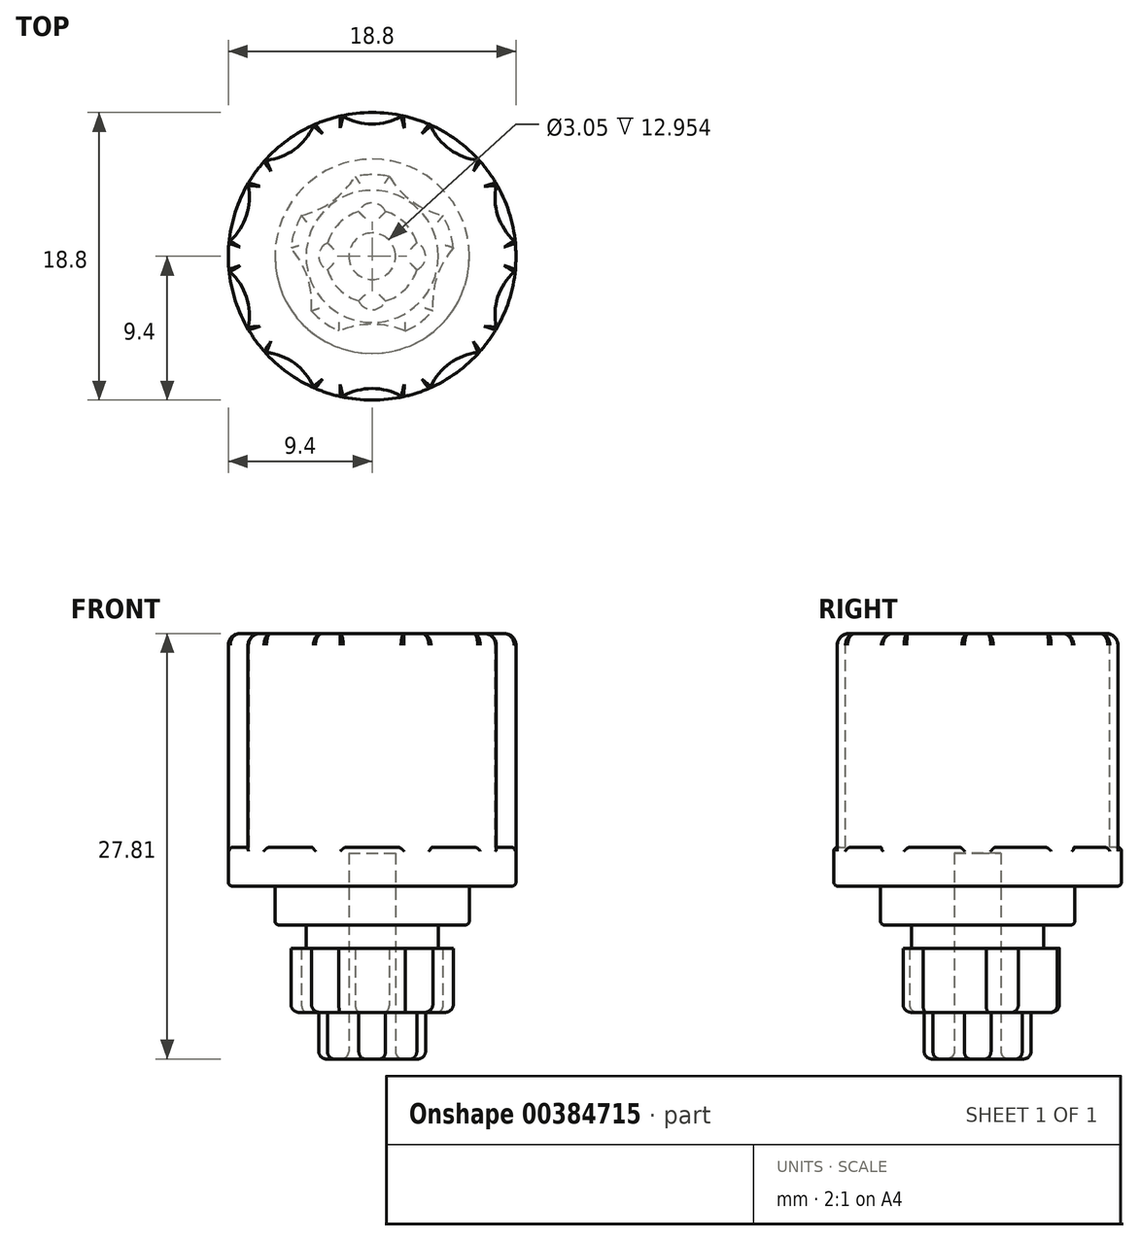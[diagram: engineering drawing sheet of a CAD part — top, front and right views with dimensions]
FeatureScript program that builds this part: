
annotation { "Feature Type Name" : "Feature", "Feature Type Description" : "" }
export const myFeature = defineFeature(function(context is Context, id is Id, definition is map)
    precondition{}
    {
        {
            var Q0;
            Q0=qCreatedBy(makeId("Top.planeOp"),FACE);
            var sketch = newSketch(context, id + "F0", { "sketchPlane" : qUnion([Q0])});
            skCircle(sketch, "E0", {"center": v(0, 0) * mm, "radius": 9.4 * mm});
            skSolve(sketch);
        }
        {
            var Q0;
            Q0=qSketchRegion(id+"F0",true);
            extrude(context, id + "F1", {"entities" : qUnion([Q0]), "depth" : 16.5 * mm});
        }
        {
            var Q0;
            Q0=makeQuery(id+"F1.opExtrude","CAP_FACE",FACE,{"disambiguationData":[OSD([sQuery(id+"F0.wireOp",EDGE,"E0")])],"isStart":false});
            var sketch = newSketch(context, id + "F2", { "sketchPlane" : qUnion([Q0])});
            skCircle(sketch, "E1.1.0", {"center": v(-7.32, 10.07) * mm, "radius": 3.81 * mm});
            skCircle(sketch, "E1.2.0", {"center": v(-11.84, 3.85) * mm, "radius": 3.81 * mm});
            skCircle(sketch, "E1.3.0", {"center": v(-11.84, -3.85) * mm, "radius": 3.81 * mm});
            skCircle(sketch, "E1.4.0", {"center": v(-7.32, -10.07) * mm, "radius": 3.81 * mm});
            skCircle(sketch, "E1.5.0", {"center": v(0, -12.45) * mm, "radius": 3.81 * mm});
            skCircle(sketch, "E1.6.0", {"center": v(7.32, -10.07) * mm, "radius": 3.81 * mm});
            skCircle(sketch, "E1.7.0", {"center": v(11.84, -3.85) * mm, "radius": 3.81 * mm});
            skCircle(sketch, "E1.8.0", {"center": v(11.84, 3.85) * mm, "radius": 3.81 * mm});
            skCircle(sketch, "E1.9.0", {"center": v(7.32, 10.07) * mm, "radius": 3.81 * mm});
            skPoint(sketch, "E1.center", {"position": v(0, 0) * mm});
            skPoint(sketch, "E2.center.orphan", {"position": v(0, 12.45) * mm});
            skCircle(sketch, "E3", {"center": v(0, 12.45) * mm, "radius": 3.81 * mm});
            skSolve(sketch);
        }
        {
            var Q0;
            Q0=qSketchRegion(id+"F2",true);
            extrude(context, id + "F3", {"entities" : qUnion([Q0]), "operationType" : NewBodyOperationType.REMOVE, "oppositeDirection" : true, "depth" : 13.97 * mm});
        }
        {
            var Q0;
            Q0=makeQuery(id+"F1.opExtrude","CAP_FACE",FACE,{"disambiguationData":[OSD([sQuery(id+"F0.wireOp",EDGE,"E0")])],"isStart":false});
            fillet(context, id + "F4", {"entities" : qUnion([Q0]), "radius" : 0.76 * mm, "tangentPropagation" : true, "allowEdgeOverflow" : false});
        }
        {
            var Q0;
            Q0=makeQuery(id+"F1.opExtrude","CAP_FACE",FACE,{"disambiguationData":[OSD([sQuery(id+"F0.wireOp",EDGE,"E0")])],"isStart":true});
            var sketch = newSketch(context, id + "F5", { "sketchPlane" : qUnion([Q0])});
            skCircle(sketch, "E4", {"center": v(0, 0) * mm, "radius": 5.33 * mm});
            skSolve(sketch);
        }
        {
            var Q0;
            Q0=qSketchRegion(id+"F5",true);
            extrude(context, id + "F6", {"entities" : qUnion([Q0]), "operationType" : NewBodyOperationType.ADD, "depth" : 8.25 * mm, "offsetDistance" : 25.4 * mm});
        }
        {
            var Q0;
            Q0=makeQuery(id+"F6.opExtrude","CAP_FACE",FACE,{"disambiguationData":[OSD([sQuery(id+"F5.wireOp",EDGE,"E4")])],"isStart":false});
            var sketch = newSketch(context, id + "F7", { "sketchPlane" : qUnion([Q0])});
            skCircle(sketch, "E5", {"center": v(0, 10.16) * mm, "radius": 5.72 * mm});
            skCircle(sketch, "E6.1.0", {"center": v(-9.66, 3.14) * mm, "radius": 5.72 * mm});
            skCircle(sketch, "E6.2.0", {"center": v(-5.97, -8.22) * mm, "radius": 5.72 * mm});
            skCircle(sketch, "E6.3.0", {"center": v(5.97, -8.22) * mm, "radius": 5.72 * mm});
            skCircle(sketch, "E6.4.0", {"center": v(9.66, 3.14) * mm, "radius": 5.72 * mm});
            skPoint(sketch, "E6.center", {"position": v(0, 0) * mm});
            skSolve(sketch);
        }
        {
            var Q0;
            Q0=qSketchRegion(id+"F7",true);
            extrude(context, id + "F8", {"entities" : qUnion([Q0]), "operationType" : NewBodyOperationType.REMOVE, "oppositeDirection" : true, "depth" : 7.62 * mm});
        }
        {
            var Q0;
            Q0=makeQuery(id+"F8.boolean.opBoolean","MERGE",FACE,{"derivedFrom":[makeQuery(id+"F1.opExtrude","CAP_FACE",FACE,{"disambiguationData":[OSD([sQuery(id+"F0.wireOp",EDGE,"E0")])],"isStart":true}),makeQuery(id+"F8.opExtrude","CAP_FACE",FACE,{"disambiguationData":[OSD([sQuery(id+"F7.wireOp",EDGE,"E5")])],"isStart":false}),makeQuery(id+"F8.opExtrude","CAP_FACE",FACE,{"disambiguationData":[OSD([sQuery(id+"F7.wireOp",EDGE,"E6.1.0")])],"isStart":false}),makeQuery(id+"F8.opExtrude","CAP_FACE",FACE,{"disambiguationData":[OSD([sQuery(id+"F7.wireOp",EDGE,"E6.2.0")])],"isStart":false}),makeQuery(id+"F8.opExtrude","CAP_FACE",FACE,{"disambiguationData":[OSD([sQuery(id+"F7.wireOp",EDGE,"E6.3.0")])],"isStart":false}),makeQuery(id+"F8.opExtrude","CAP_FACE",FACE,{"disambiguationData":[OSD([sQuery(id+"F7.wireOp",EDGE,"E6.4.0")])],"isStart":false})]});
            var sketch = newSketch(context, id + "F9", { "sketchPlane" : qUnion([Q0])});
            skCircle(sketch, "E7", {"center": v(0, 0) * mm, "radius": 6.22 * mm});
            skCircle(sketch, "E8", {"center": v(0, 0) * mm, "radius": 4.32 * mm});
            skSolve(sketch);
        }
        {
            var Q0;
            Q0=qSketchRegion(id+"F9",true);
            extrude(context, id + "F10", {"entities" : qUnion([Q0]), "operationType" : NewBodyOperationType.REMOVE, "depth" : 4.06 * mm, "offsetDistance" : 25.4 * mm});
        }
        {
            var Q0;
            Q0=makeQuery(id+"F10.boolean.opBoolean","MERGE",FACE,{"derivedFrom":[makeQuery(id+"F1.opExtrude","CAP_FACE",FACE,{"disambiguationData":[OSD([sQuery(id+"F0.wireOp",EDGE,"E0")])],"isStart":true}),makeQuery(id+"F10.opExtrude","CAP_FACE",FACE,{"disambiguationData":[OSD([sQuery(id+"F9.wireOp",EDGE,"E7"),sQuery(id+"F9.wireOp",EDGE,"E8")])],"isStart":true})]});
            var sketch = newSketch(context, id + "F11", { "sketchPlane" : qUnion([Q0])});
            skCircle(sketch, "E9", {"center": v(0, 0) * mm, "radius": 6.35 * mm});
            skSolve(sketch);
        }
        {
            var Q0;
            Q0=qSketchRegion(id+"F11",true);
            extrude(context, id + "F12", {"entities" : qUnion([Q0]), "operationType" : NewBodyOperationType.ADD, "depth" : 2.54 * mm, "offsetDistance" : 25.4 * mm});
        }
        {
            var Q0;
            Q0=makeQuery(id+"F6.opExtrude","CAP_FACE",FACE,{"disambiguationData":[OSD([sQuery(id+"F5.wireOp",EDGE,"E4")])],"isStart":false});
            fillet(context, id + "F13", {"entities" : qUnion([Q0]), "radius" : 0.5 * mm, "tangentPropagation" : true, "allowEdgeOverflow" : false});
        }
        {
            var Q0;
            Q0=makeQuery(id+"F12.opExtrude","CAP_EDGE",EDGE,{"disambiguationData":[OSD([sQuery(id+"F11.wireOp",EDGE,"E9")])],"isStart":false});
            var Q1;
            Q1=makeQuery(id+"F1.opExtrude","CAP_EDGE",EDGE,{"disambiguationData":[OSD([sQuery(id+"F0.wireOp",EDGE,"E0")])],"isStart":true});
            var Q2;
            Q2=makeQuery(id+"F3.boolean.opBoolean","INTERSECT",EDGE,{"derivedFrom":[makeQuery(id+"F1.opExtrude","SWEPT_FACE",FACE,{"disambiguationData":[OSD([sQuery(id+"F0.wireOp",EDGE,"E0")])]}),makeQuery(id+"F3.opExtrude","CAP_FACE",FACE,{"disambiguationData":[OSD([sQuery(id+"F2.wireOp",EDGE,"E1.4.0")])],"isStart":false})]});
            var Q3;
            Q3=makeQuery(id+"F3.boolean.opBoolean","INTERSECT",EDGE,{"derivedFrom":[makeQuery(id+"F1.opExtrude","SWEPT_FACE",FACE,{"disambiguationData":[OSD([sQuery(id+"F0.wireOp",EDGE,"E0")])]}),makeQuery(id+"F3.opExtrude","CAP_FACE",FACE,{"disambiguationData":[OSD([sQuery(id+"F2.wireOp",EDGE,"E1.5.0")])],"isStart":false})]});
            var Q4;
            Q4=makeQuery(id+"F3.boolean.opBoolean","INTERSECT",EDGE,{"disambiguationData":[OD(0.0)],"derivedFrom":[makeQuery(id+"F1.opExtrude","SWEPT_FACE",FACE,{"disambiguationData":[OSD([sQuery(id+"F0.wireOp",EDGE,"E0")])]}),makeQuery(id+"F3.opExtrude","SWEPT_FACE",FACE,{"disambiguationData":[OSD([sQuery(id+"F2.wireOp",EDGE,"E1.4.0")])]})]});
            var Q5;
            Q5=makeQuery(id+"F3.boolean.opBoolean","INTERSECT",EDGE,{"disambiguationData":[OD(1.0)],"derivedFrom":[makeQuery(id+"F1.opExtrude","SWEPT_FACE",FACE,{"disambiguationData":[OSD([sQuery(id+"F0.wireOp",EDGE,"E0")])]}),makeQuery(id+"F3.opExtrude","SWEPT_FACE",FACE,{"disambiguationData":[OSD([sQuery(id+"F2.wireOp",EDGE,"E1.4.0")])]})]});
            var Q6;
            Q6=makeQuery(id+"F3.boolean.opBoolean","INTERSECT",EDGE,{"disambiguationData":[OD(0.0)],"derivedFrom":[makeQuery(id+"F1.opExtrude","SWEPT_FACE",FACE,{"disambiguationData":[OSD([sQuery(id+"F0.wireOp",EDGE,"E0")])]}),makeQuery(id+"F3.opExtrude","SWEPT_FACE",FACE,{"disambiguationData":[OSD([sQuery(id+"F2.wireOp",EDGE,"E1.5.0")])]})]});
            var Q7;
            Q7=makeQuery(id+"F3.boolean.opBoolean","INTERSECT",EDGE,{"disambiguationData":[OD(1.0)],"derivedFrom":[makeQuery(id+"F1.opExtrude","SWEPT_FACE",FACE,{"disambiguationData":[OSD([sQuery(id+"F0.wireOp",EDGE,"E0")])]}),makeQuery(id+"F3.opExtrude","SWEPT_FACE",FACE,{"disambiguationData":[OSD([sQuery(id+"F2.wireOp",EDGE,"E1.5.0")])]})]});
            var Q8;
            Q8=makeQuery(id+"F3.boolean.opBoolean","INTERSECT",EDGE,{"disambiguationData":[OD(0.0)],"derivedFrom":[makeQuery(id+"F1.opExtrude","SWEPT_FACE",FACE,{"disambiguationData":[OSD([sQuery(id+"F0.wireOp",EDGE,"E0")])]}),makeQuery(id+"F3.opExtrude","SWEPT_FACE",FACE,{"disambiguationData":[OSD([sQuery(id+"F2.wireOp",EDGE,"E1.6.0")])]})]});
            var Q9;
            Q9=makeQuery(id+"F3.boolean.opBoolean","INTERSECT",EDGE,{"derivedFrom":[makeQuery(id+"F1.opExtrude","SWEPT_FACE",FACE,{"disambiguationData":[OSD([sQuery(id+"F0.wireOp",EDGE,"E0")])]}),makeQuery(id+"F3.opExtrude","CAP_FACE",FACE,{"disambiguationData":[OSD([sQuery(id+"F2.wireOp",EDGE,"E1.6.0")])],"isStart":false})]});
            var Q10;
            Q10=makeQuery(id+"F3.boolean.opBoolean","INTERSECT",EDGE,{"disambiguationData":[OD(1.0)],"derivedFrom":[makeQuery(id+"F1.opExtrude","SWEPT_FACE",FACE,{"disambiguationData":[OSD([sQuery(id+"F0.wireOp",EDGE,"E0")])]}),makeQuery(id+"F3.opExtrude","SWEPT_FACE",FACE,{"disambiguationData":[OSD([sQuery(id+"F2.wireOp",EDGE,"E1.6.0")])]})]});
            var Q11;
            Q11=makeQuery(id+"F3.boolean.opBoolean","INTERSECT",EDGE,{"disambiguationData":[OD(0.0)],"derivedFrom":[makeQuery(id+"F1.opExtrude","SWEPT_FACE",FACE,{"disambiguationData":[OSD([sQuery(id+"F0.wireOp",EDGE,"E0")])]}),makeQuery(id+"F3.opExtrude","SWEPT_FACE",FACE,{"disambiguationData":[OSD([sQuery(id+"F2.wireOp",EDGE,"E1.7.0")])]})]});
            var Q12;
            Q12=makeQuery(id+"F3.boolean.opBoolean","INTERSECT",EDGE,{"derivedFrom":[makeQuery(id+"F1.opExtrude","SWEPT_FACE",FACE,{"disambiguationData":[OSD([sQuery(id+"F0.wireOp",EDGE,"E0")])]}),makeQuery(id+"F3.opExtrude","CAP_FACE",FACE,{"disambiguationData":[OSD([sQuery(id+"F2.wireOp",EDGE,"E1.7.0")])],"isStart":false})]});
            var Q13;
            Q13=makeQuery(id+"F3.boolean.opBoolean","INTERSECT",EDGE,{"disambiguationData":[OD(1.0)],"derivedFrom":[makeQuery(id+"F1.opExtrude","SWEPT_FACE",FACE,{"disambiguationData":[OSD([sQuery(id+"F0.wireOp",EDGE,"E0")])]}),makeQuery(id+"F3.opExtrude","SWEPT_FACE",FACE,{"disambiguationData":[OSD([sQuery(id+"F2.wireOp",EDGE,"E1.7.0")])]})]});
            var Q14;
            Q14=makeQuery(id+"F3.boolean.opBoolean","INTERSECT",EDGE,{"derivedFrom":[makeQuery(id+"F1.opExtrude","SWEPT_FACE",FACE,{"disambiguationData":[OSD([sQuery(id+"F0.wireOp",EDGE,"E0")])]}),makeQuery(id+"F3.opExtrude","CAP_FACE",FACE,{"disambiguationData":[OSD([sQuery(id+"F2.wireOp",EDGE,"E1.8.0")])],"isStart":false})]});
            var Q15;
            Q15=makeQuery(id+"F3.boolean.opBoolean","INTERSECT",EDGE,{"disambiguationData":[OD(0.0)],"derivedFrom":[makeQuery(id+"F1.opExtrude","SWEPT_FACE",FACE,{"disambiguationData":[OSD([sQuery(id+"F0.wireOp",EDGE,"E0")])]}),makeQuery(id+"F3.opExtrude","SWEPT_FACE",FACE,{"disambiguationData":[OSD([sQuery(id+"F2.wireOp",EDGE,"E1.8.0")])]})]});
            var Q16;
            Q16=makeQuery(id+"F3.boolean.opBoolean","INTERSECT",EDGE,{"disambiguationData":[OD(1.0)],"derivedFrom":[makeQuery(id+"F1.opExtrude","SWEPT_FACE",FACE,{"disambiguationData":[OSD([sQuery(id+"F0.wireOp",EDGE,"E0")])]}),makeQuery(id+"F3.opExtrude","SWEPT_FACE",FACE,{"disambiguationData":[OSD([sQuery(id+"F2.wireOp",EDGE,"E1.8.0")])]})]});
            var Q17;
            Q17=makeQuery(id+"F3.boolean.opBoolean","INTERSECT",EDGE,{"disambiguationData":[OD(1.0)],"derivedFrom":[makeQuery(id+"F1.opExtrude","SWEPT_FACE",FACE,{"disambiguationData":[OSD([sQuery(id+"F0.wireOp",EDGE,"E0")])]}),makeQuery(id+"F3.opExtrude","SWEPT_FACE",FACE,{"disambiguationData":[OSD([sQuery(id+"F2.wireOp",EDGE,"E1.9.0")])]})]});
            var Q18;
            Q18=makeQuery(id+"F3.boolean.opBoolean","INTERSECT",EDGE,{"derivedFrom":[makeQuery(id+"F1.opExtrude","SWEPT_FACE",FACE,{"disambiguationData":[OSD([sQuery(id+"F0.wireOp",EDGE,"E0")])]}),makeQuery(id+"F3.opExtrude","CAP_FACE",FACE,{"disambiguationData":[OSD([sQuery(id+"F2.wireOp",EDGE,"E1.9.0")])],"isStart":false})]});
            var Q19;
            Q19=makeQuery(id+"F3.boolean.opBoolean","INTERSECT",EDGE,{"disambiguationData":[OD(0.0)],"derivedFrom":[makeQuery(id+"F1.opExtrude","SWEPT_FACE",FACE,{"disambiguationData":[OSD([sQuery(id+"F0.wireOp",EDGE,"E0")])]}),makeQuery(id+"F3.opExtrude","SWEPT_FACE",FACE,{"disambiguationData":[OSD([sQuery(id+"F2.wireOp",EDGE,"E1.9.0")])]})]});
            var Q20;
            Q20=makeQuery(id+"F3.boolean.opBoolean","INTERSECT",EDGE,{"disambiguationData":[OD(1.0)],"derivedFrom":[makeQuery(id+"F1.opExtrude","SWEPT_FACE",FACE,{"disambiguationData":[OSD([sQuery(id+"F0.wireOp",EDGE,"E0")])]}),makeQuery(id+"F3.opExtrude","SWEPT_FACE",FACE,{"disambiguationData":[OSD([sQuery(id+"F2.wireOp",EDGE,"E3")])]})]});
            var Q21;
            Q21=makeQuery(id+"F3.boolean.opBoolean","INTERSECT",EDGE,{"derivedFrom":[makeQuery(id+"F1.opExtrude","SWEPT_FACE",FACE,{"disambiguationData":[OSD([sQuery(id+"F0.wireOp",EDGE,"E0")])]}),makeQuery(id+"F3.opExtrude","CAP_FACE",FACE,{"disambiguationData":[OSD([sQuery(id+"F2.wireOp",EDGE,"E3")])],"isStart":false})]});
            var Q22;
            Q22=makeQuery(id+"F3.boolean.opBoolean","INTERSECT",EDGE,{"disambiguationData":[OD(0.0)],"derivedFrom":[makeQuery(id+"F1.opExtrude","SWEPT_FACE",FACE,{"disambiguationData":[OSD([sQuery(id+"F0.wireOp",EDGE,"E0")])]}),makeQuery(id+"F3.opExtrude","SWEPT_FACE",FACE,{"disambiguationData":[OSD([sQuery(id+"F2.wireOp",EDGE,"E3")])]})]});
            var Q23;
            Q23=makeQuery(id+"F3.boolean.opBoolean","INTERSECT",EDGE,{"derivedFrom":[makeQuery(id+"F1.opExtrude","SWEPT_FACE",FACE,{"disambiguationData":[OSD([sQuery(id+"F0.wireOp",EDGE,"E0")])]}),makeQuery(id+"F3.opExtrude","CAP_FACE",FACE,{"disambiguationData":[OSD([sQuery(id+"F2.wireOp",EDGE,"E1.1.0")])],"isStart":false})]});
            var Q24;
            Q24=makeQuery(id+"F3.boolean.opBoolean","INTERSECT",EDGE,{"disambiguationData":[OD(1.0)],"derivedFrom":[makeQuery(id+"F1.opExtrude","SWEPT_FACE",FACE,{"disambiguationData":[OSD([sQuery(id+"F0.wireOp",EDGE,"E0")])]}),makeQuery(id+"F3.opExtrude","SWEPT_FACE",FACE,{"disambiguationData":[OSD([sQuery(id+"F2.wireOp",EDGE,"E1.1.0")])]})]});
            var Q25;
            Q25=makeQuery(id+"F3.boolean.opBoolean","INTERSECT",EDGE,{"disambiguationData":[OD(0.0)],"derivedFrom":[makeQuery(id+"F1.opExtrude","SWEPT_FACE",FACE,{"disambiguationData":[OSD([sQuery(id+"F0.wireOp",EDGE,"E0")])]}),makeQuery(id+"F3.opExtrude","SWEPT_FACE",FACE,{"disambiguationData":[OSD([sQuery(id+"F2.wireOp",EDGE,"E1.1.0")])]})]});
            var Q26;
            Q26=makeQuery(id+"F3.boolean.opBoolean","INTERSECT",EDGE,{"disambiguationData":[OD(1.0)],"derivedFrom":[makeQuery(id+"F1.opExtrude","SWEPT_FACE",FACE,{"disambiguationData":[OSD([sQuery(id+"F0.wireOp",EDGE,"E0")])]}),makeQuery(id+"F3.opExtrude","SWEPT_FACE",FACE,{"disambiguationData":[OSD([sQuery(id+"F2.wireOp",EDGE,"E1.2.0")])]})]});
            var Q27;
            Q27=makeQuery(id+"F3.boolean.opBoolean","INTERSECT",EDGE,{"derivedFrom":[makeQuery(id+"F1.opExtrude","SWEPT_FACE",FACE,{"disambiguationData":[OSD([sQuery(id+"F0.wireOp",EDGE,"E0")])]}),makeQuery(id+"F3.opExtrude","CAP_FACE",FACE,{"disambiguationData":[OSD([sQuery(id+"F2.wireOp",EDGE,"E1.2.0")])],"isStart":false})]});
            var Q28;
            Q28=makeQuery(id+"F3.boolean.opBoolean","INTERSECT",EDGE,{"disambiguationData":[OD(0.0)],"derivedFrom":[makeQuery(id+"F1.opExtrude","SWEPT_FACE",FACE,{"disambiguationData":[OSD([sQuery(id+"F0.wireOp",EDGE,"E0")])]}),makeQuery(id+"F3.opExtrude","SWEPT_FACE",FACE,{"disambiguationData":[OSD([sQuery(id+"F2.wireOp",EDGE,"E1.2.0")])]})]});
            var Q29;
            Q29=makeQuery(id+"F3.boolean.opBoolean","INTERSECT",EDGE,{"disambiguationData":[OD(1.0)],"derivedFrom":[makeQuery(id+"F1.opExtrude","SWEPT_FACE",FACE,{"disambiguationData":[OSD([sQuery(id+"F0.wireOp",EDGE,"E0")])]}),makeQuery(id+"F3.opExtrude","SWEPT_FACE",FACE,{"disambiguationData":[OSD([sQuery(id+"F2.wireOp",EDGE,"E1.3.0")])]})]});
            var Q30;
            Q30=makeQuery(id+"F3.boolean.opBoolean","INTERSECT",EDGE,{"derivedFrom":[makeQuery(id+"F1.opExtrude","SWEPT_FACE",FACE,{"disambiguationData":[OSD([sQuery(id+"F0.wireOp",EDGE,"E0")])]}),makeQuery(id+"F3.opExtrude","CAP_FACE",FACE,{"disambiguationData":[OSD([sQuery(id+"F2.wireOp",EDGE,"E1.3.0")])],"isStart":false})]});
            var Q31;
            Q31=makeQuery(id+"F3.boolean.opBoolean","INTERSECT",EDGE,{"disambiguationData":[OD(0.0)],"derivedFrom":[makeQuery(id+"F1.opExtrude","SWEPT_FACE",FACE,{"disambiguationData":[OSD([sQuery(id+"F0.wireOp",EDGE,"E0")])]}),makeQuery(id+"F3.opExtrude","SWEPT_FACE",FACE,{"disambiguationData":[OSD([sQuery(id+"F2.wireOp",EDGE,"E1.3.0")])]})]});
            fillet(context, id + "F14", {"entities" : qUnion([Q0, Q1, Q2, Q3, Q4, Q5, Q6, Q7, Q8, Q9, Q10, Q11, Q12, Q13, Q14, Q15, Q16, Q17, Q18, Q19, Q20, Q21, Q22, Q23, Q24, Q25, Q26, Q27, Q28, Q29, Q30, Q31]), "radius" : 0.25 * mm, "tangentPropagation" : true, "allowEdgeOverflow" : false});
        }
        {
            var Q0;
            Q0=makeQuery(id+"F6.opExtrude","CAP_FACE",FACE,{"disambiguationData":[OSD([sQuery(id+"F5.wireOp",EDGE,"E4")])],"isStart":false});
            var sketch = newSketch(context, id + "F15", { "sketchPlane" : qUnion([Q0])});
            skCircle(sketch, "E10", {"center": v(0, 0) * mm, "radius": 1.52 * mm});
            skSolve(sketch);
        }
        {
            var Q0;
            Q0=qSketchRegion(id+"F15",true);
            extrude(context, id + "F16", {"entities" : qUnion([Q0]), "operationType" : NewBodyOperationType.REMOVE, "oppositeDirection" : true, "depth" : 10.4 * mm, "offsetDistance" : 25.4 * mm});
        }
        {
            var Q0;
            Q0=makeQuery(id+"F6.opExtrude","CAP_FACE",FACE,{"disambiguationData":[OSD([sQuery(id+"F5.wireOp",EDGE,"E4")])],"isStart":false});
            var sketch = newSketch(context, id + "F17", { "sketchPlane" : qUnion([Q0])});
            skArc(sketch, "E11", {"start": v(0.87, -2.92) * mm, "mid": v(0, 3.05) * mm, "end": v(-0.87, -2.92) * mm});
            skArc(sketch, "E12", {"start": v(-0.87, -2.92) * mm, "mid": v(0, -3.5) * mm, "end": v(0.87, -2.92) * mm});
            skCircle(sketch, "E13", {"center": v(0, 0) * mm, "radius": 1.52 * mm});
            skArc(sketch, "E14.1.0", {"start": v(2.92, -0.87) * mm, "mid": v(3.5, 0) * mm, "end": v(2.92, 0.87) * mm});
            skArc(sketch, "E15.2.2.0", {"start": v(0.87, 2.92) * mm, "mid": v(0, 3.5) * mm, "end": v(-0.87, 2.92) * mm});
            skArc(sketch, "E15.2.3.0", {"start": v(-2.92, 0.87) * mm, "mid": v(-3.5, 0) * mm, "end": v(-2.92, -0.87) * mm});
            skSolve(sketch);
        }
        {
            var Q0;
            Q0 = qSketchRegion(id + "F17", true);
            extrude(context, id + "F18", {"entities" : qUnion([Q0]), "operationType" : NewBodyOperationType.ADD, "depth" : 3.05 * mm, "offsetDistance" : 25.4 * mm});
        }
        {
            var Q0;
            Q0=makeQuery(id+"F18.opExtrude","CAP_FACE",FACE,{"disambiguationData":[OSD([sQuery(id+"F17.wireOp",EDGE,"E11"),sQuery(id+"F17.wireOp",EDGE,"E12"),sQuery(id+"F17.wireOp",EDGE,"E13")])],"isStart":false});
            fillet(context, id + "F19", {"entities" : qUnion([Q0]), "radius" : 0.5 * mm, "tangentPropagation" : true, "allowEdgeOverflow" : false});
        }
    });
